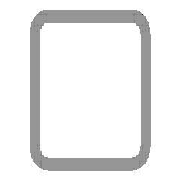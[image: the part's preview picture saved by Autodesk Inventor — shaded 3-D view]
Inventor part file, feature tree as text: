
AUTODESK INVENTOR PART (.ipt)
format: ipt  version: 2025 (Build 290162010, 162A)  size: 133,120 bytes
history: native  units: mm (DEFAULTED — no unit token found)
features: other x4, sketch x1, plane x1
ambient origin geometry x8: Origin, YZ Plane, XZ Plane, XY Plane, X Axis, Y Axis, Z Axis, Center Point
bodies: Solid1 (feature_tree), Body (feature_tree)
feature tree (6):
  parser-record x1  (decoder bookkeeping rows leaked as tree rows — omitted from the tree; the rows remain in map.json)
  other  "Driven Length"
  other  "Start Plane"
  other  "End Plane"
  sketch  "Sketch3"  dims[d3=1120.0mm d4=0.0mm d7=6.0mm d9=80.0mm d11=80.0mm d12=3.0mm d13=40.0mm d14=1160.0mm d15=40.0mm d16=40.0mm d17=90.0deg d18=1120.0mm]
  plane  "Work Plane3"
